# Revit family: Toilet_Seat-Round_Closed_Front-KOHLER-Stonewood-K-20467
name_source: partatom
category: Specialty Equipment
units: mm (PartAtom-declared; Revit-internal decimal feet)

## family parameters
Cut with Voids When Loaded = No
Host = Face
OmniClass Number = 23.31.19.19.17
OmniClass Title = Water Closet Seats
Part Type = Normal
Room Calculation Point = No
Round Connector Dimension = Use Diameter
Shared = No

## types (2) — shared parameters
ADA Compliant = No
Assembly Code = C1030200
Date Modified = 04/12/2023
Description = Quiet Close round-front toilet seat
Height = 2 1/8"
Length = 17 7/16"
Manufacturer = Kohler Co.
Master Format 2014 = 10 28 00
Master Format 2014 Name = Toilet, Bath, and Laundry Accessories
Material = Molded Wood
Product Documentation Link = https://www.us.kohler.com
Product Name = Stonewood
Product Page URL = http://www.us.kohler.com
URL = https://www.us.kohler.com
WaterSense Certified = No
Width = 14 3/16"

## per-type parameters (varying)
| type | Default Elevation | Finish | Model | Type |
| 0-White | 15" | Kohler-Wood-Molded-0-White | K-20467-0 | 1 |
| 96-Biscuit | 42" | Kohler-Wood-Molded-96-Biscuit | K-20467-96 | 2 |

## geometry (parser evidence)
native form markers: Sweep x6
no freeform markers — native parametric forms only
